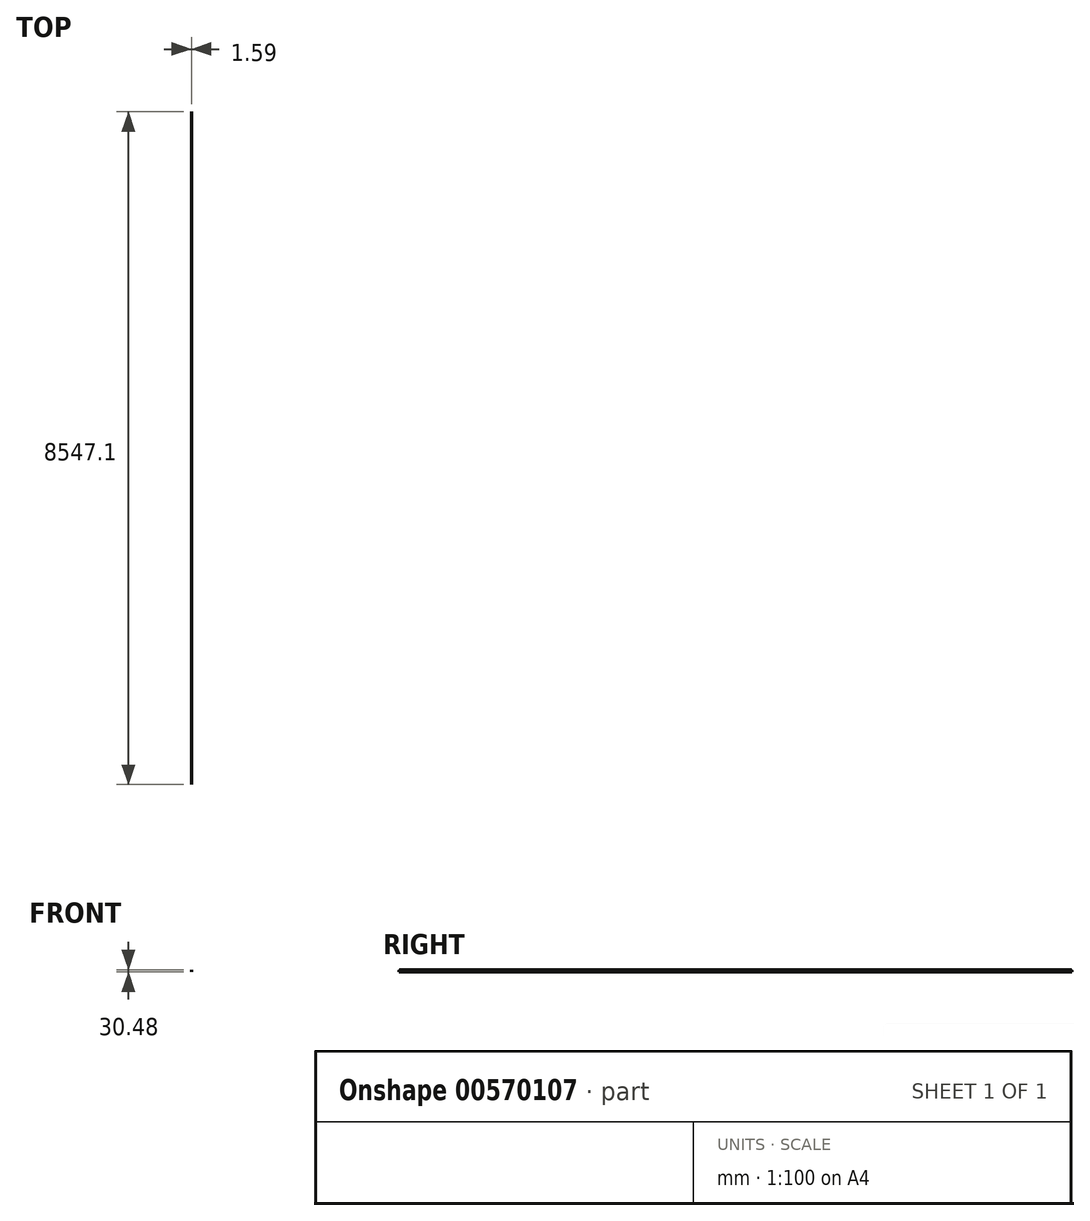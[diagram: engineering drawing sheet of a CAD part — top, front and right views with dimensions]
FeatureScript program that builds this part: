
annotation { "Feature Type Name" : "Feature", "Feature Type Description" : "" }
export const myFeature = defineFeature(function(context is Context, id is Id, definition is map)
    precondition{}
    {
        {
            var Q0;
            Q0=qCreatedBy(makeId("Front.planeOp"),FACE);
            var sketch = newSketch(context, id + "F0", { "sketchPlane" : qUnion([Q0])});
            skLineSegment(sketch, "E0.bottom", {"start": v(0, 0) * mm, "end": v(1.59, 0) * mm});
            skLineSegment(sketch, "E0.top", {"start": v(0, -30.48) * mm, "end": v(1.59, -30.48) * mm});
            skLineSegment(sketch, "E0.left", {"start": v(0, 0) * mm, "end": v(0, -30.48) * mm});
            skLineSegment(sketch, "E0.right", {"start": v(1.59, 0) * mm, "end": v(1.59, -30.48) * mm});
            skSolve(sketch);
        }
        {
            var Q0;
            Q0 = qSketchRegion(id + "F0", true);
            extrude(context, id + "F1", {"entities" : qUnion([Q0]), "depth" : 8547.1 * mm, "offsetDistance" : 25.4 * mm});
        }
        {
            var Q0;
            Q0=makeQuery(id+"F1.opExtrude","SWEPT_FACE",FACE,{"disambiguationData":[OSD([sQuery(id+"F0.wireOp",EDGE,"E0.bottom")])]});
            var sketch = newSketch(context, id + "F2", { "sketchPlane" : qUnion([Q0])});
            skLineSegment(sketch, "E1.0", {"start": v(0, -7.14) * mm, "end": v(1.59, -7.14) * mm});
            skLineSegment(sketch, "E2.0", {"start": v(0, -8539.96) * mm, "end": v(1.59, -8539.96) * mm});
            skSolve(sketch);
        }
        {
            var Q0;
            {var subQ0=sQuery(id+"F2.wireOp",EDGE,"E2.0");Q0=makeQuery(id+"F2.imprint","IMPRINT",FACE,{"disambiguationData":[TD([[makeQuery(id+"F2.imprint","IMPRINT",EDGE,{"derivedFrom":subQ0}),-1.0]])]});}
            var Q1;
            {var subQ0=sQuery(id+"F2.wireOp",EDGE,"E1.0");Q1=makeQuery(id+"F2.imprint","IMPRINT",FACE,{"disambiguationData":[TD([[makeQuery(id+"F2.imprint","IMPRINT",EDGE,{"derivedFrom":subQ0}),1.0]])]});}
            extrude(context, id + "F3", {"entities" : qUnion([Q0, Q1]), "operationType" : NewBodyOperationType.REMOVE, "oppositeDirection" : true, "depth" : 6.35 * mm, "offsetDistance" : 25.4 * mm});
        }
    });
